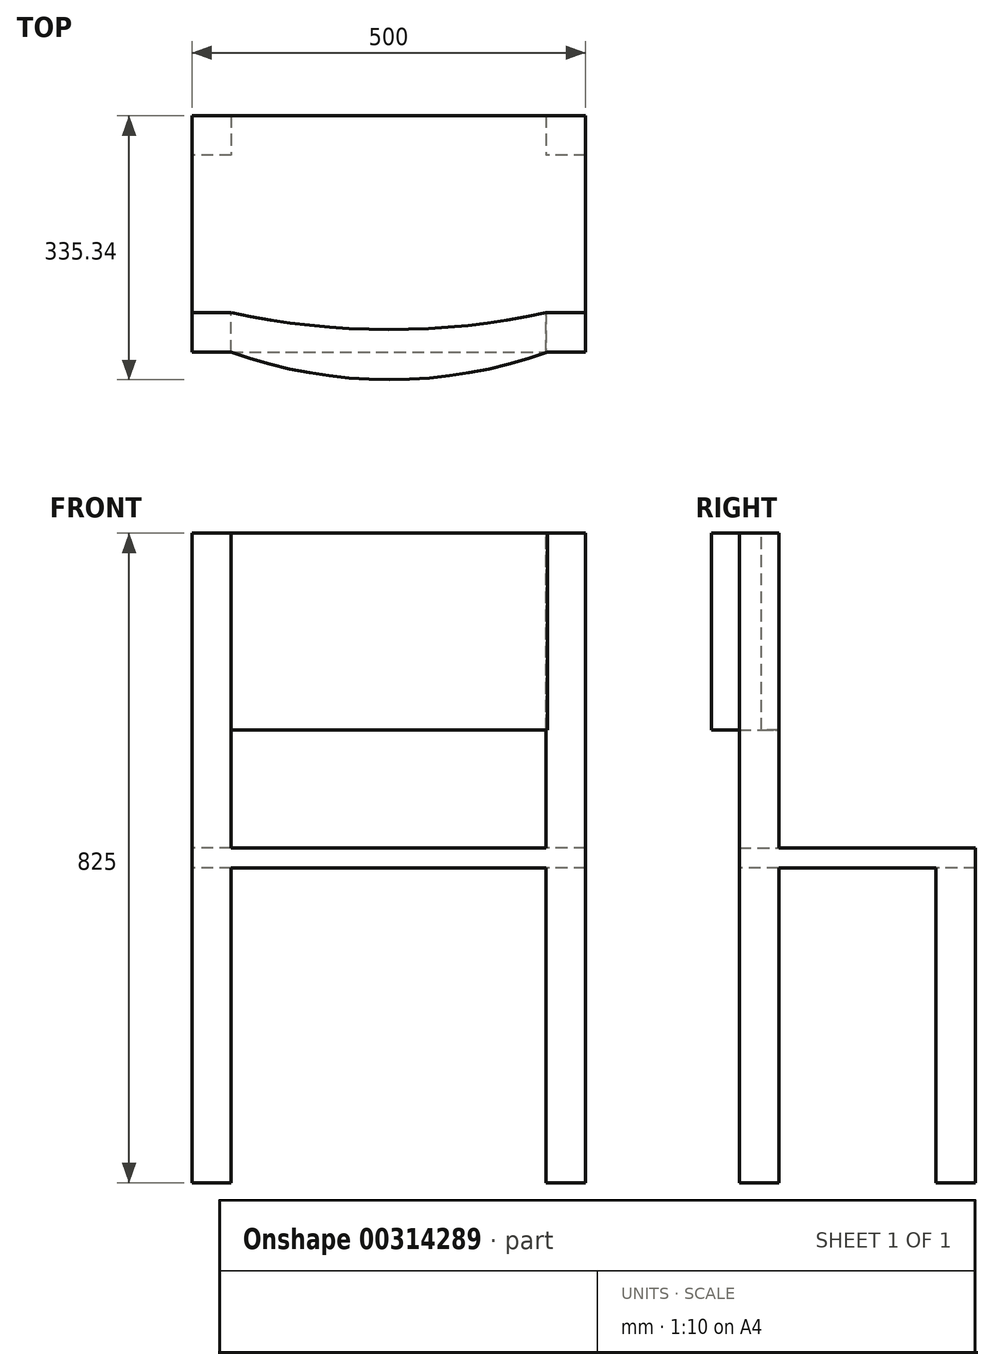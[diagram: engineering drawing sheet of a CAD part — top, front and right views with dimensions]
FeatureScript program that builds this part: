
annotation { "Feature Type Name" : "Feature", "Feature Type Description" : "" }
export const myFeature = defineFeature(function(context is Context, id is Id, definition is map)
    precondition{}
    {
        {
            var Q0;
            Q0=qCreatedBy(makeId("Top.planeOp"),FACE);
            var sketch = newSketch(context, id + "F0", { "sketchPlane" : qUnion([Q0])});
            skLineSegment(sketch, "E0.bottom", {"start": v(-295.12, 76.38) * mm, "end": v(204.88, 76.38) * mm});
            skLineSegment(sketch, "E0.top", {"start": v(-295.12, -223.62) * mm, "end": v(204.88, -223.62) * mm});
            skLineSegment(sketch, "E0.left", {"start": v(-295.12, 76.38) * mm, "end": v(-295.12, -223.62) * mm});
            skLineSegment(sketch, "E0.right", {"start": v(204.88, 76.38) * mm, "end": v(204.88, -223.62) * mm});
            skSolve(sketch);
        }
        {
            var Q0;
            Q0=makeQuery(id+"F0.imprint","IMPRINT",FACE,{"disambiguationData":[TD([[makeQuery(id+"F0.imprint","IMPRINT",EDGE,{"derivedFrom":sQuery(id+"F0.wireOp",EDGE,"E0.bottom")}),-1.0]])]});
            extrude(context, id + "F1", {"entities" : qUnion([Q0]), "depth" : 25 * mm});
        }
        {
            var Q0;
            Q0=makeQuery(id+"F1.opExtrude","CAP_FACE",FACE,{"disambiguationData":[OSD([sQuery(id+"F0.wireOp",EDGE,"E0.bottom"),sQuery(id+"F0.wireOp",EDGE,"E0.top"),sQuery(id+"F0.wireOp",EDGE,"E0.left"),sQuery(id+"F0.wireOp",EDGE,"E0.right")])],"isStart":true});
            var sketch = newSketch(context, id + "F2", { "sketchPlane" : qUnion([Q0])});
            skLineSegment(sketch, "E1.bottom", {"start": v(204.88, -76.38) * mm, "end": v(154.88, -76.38) * mm});
            skLineSegment(sketch, "E1.top", {"start": v(204.88, -26.38) * mm, "end": v(154.88, -26.38) * mm});
            skLineSegment(sketch, "E1.left", {"start": v(204.88, -76.38) * mm, "end": v(204.88, -26.38) * mm});
            skLineSegment(sketch, "E1.right", {"start": v(154.88, -76.38) * mm, "end": v(154.88, -26.38) * mm});
            skLineSegment(sketch, "E2.bottom", {"start": v(-245.12, -76.38) * mm, "end": v(-295.12, -76.38) * mm});
            skLineSegment(sketch, "E2.top", {"start": v(-245.12, -26.38) * mm, "end": v(-295.12, -26.38) * mm});
            skLineSegment(sketch, "E2.left", {"start": v(-245.12, -76.38) * mm, "end": v(-245.12, -26.38) * mm});
            skLineSegment(sketch, "E2.right", {"start": v(-295.12, -76.38) * mm, "end": v(-295.12, -26.38) * mm});
            skLineSegment(sketch, "E3.bottom", {"start": v(204.88, 173.62) * mm, "end": v(154.88, 173.62) * mm});
            skLineSegment(sketch, "E3.top", {"start": v(204.88, 223.62) * mm, "end": v(154.88, 223.62) * mm});
            skLineSegment(sketch, "E3.left", {"start": v(204.88, 173.62) * mm, "end": v(204.88, 223.62) * mm});
            skLineSegment(sketch, "E3.right", {"start": v(154.88, 173.62) * mm, "end": v(154.88, 223.62) * mm});
            skLineSegment(sketch, "E4.bottom", {"start": v(-245.12, 173.62) * mm, "end": v(-295.12, 173.62) * mm});
            skLineSegment(sketch, "E4.top", {"start": v(-245.12, 223.62) * mm, "end": v(-295.12, 223.62) * mm});
            skLineSegment(sketch, "E4.left", {"start": v(-245.12, 173.62) * mm, "end": v(-245.12, 223.62) * mm});
            skLineSegment(sketch, "E4.right", {"start": v(-295.12, 173.62) * mm, "end": v(-295.12, 223.62) * mm});
            skSolve(sketch);
        }
        {
            var Q0;
            Q0=makeQuery(id+"F2.imprint","IMPRINT",FACE,{"disambiguationData":[TD([[makeQuery(id+"F2.imprint","IMPRINT",EDGE,{"derivedFrom":sQuery(id+"F2.wireOp",EDGE,"E1.bottom")}),1.0]])]});
            var Q1;
            Q1=makeQuery(id+"F2.imprint","IMPRINT",FACE,{"disambiguationData":[TD([[makeQuery(id+"F2.imprint","IMPRINT",EDGE,{"derivedFrom":sQuery(id+"F2.wireOp",EDGE,"E3.bottom")}),-1.0]])]});
            var Q2;
            Q2=makeQuery(id+"F2.imprint","IMPRINT",FACE,{"disambiguationData":[TD([[makeQuery(id+"F2.imprint","IMPRINT",EDGE,{"derivedFrom":sQuery(id+"F2.wireOp",EDGE,"E2.bottom")}),1.0]])]});
            var Q3;
            Q3=makeQuery(id+"F2.imprint","IMPRINT",FACE,{"disambiguationData":[TD([[makeQuery(id+"F2.imprint","IMPRINT",EDGE,{"derivedFrom":sQuery(id+"F2.wireOp",EDGE,"E4.bottom")}),-1.0]])]});
            extrude(context, id + "F3", {"entities" : qUnion([Q0, Q1, Q2, Q3]), "operationType" : NewBodyOperationType.ADD, "depth" : 400 * mm});
        }
        {
            var Q0;
            Q0=makeQuery(id+"F1.opExtrude","CAP_FACE",FACE,{"disambiguationData":[OSD([sQuery(id+"F0.wireOp",EDGE,"E0.bottom"),sQuery(id+"F0.wireOp",EDGE,"E0.top"),sQuery(id+"F0.wireOp",EDGE,"E0.left"),sQuery(id+"F0.wireOp",EDGE,"E0.right")])],"isStart":false});
            var sketch = newSketch(context, id + "F4", { "sketchPlane" : qUnion([Q0])});
            skLineSegment(sketch, "E5.bottom", {"start": v(204.88, -223.62) * mm, "end": v(154.88, -223.62) * mm});
            skLineSegment(sketch, "E5.top", {"start": v(204.88, -173.62) * mm, "end": v(154.88, -173.62) * mm});
            skLineSegment(sketch, "E5.left", {"start": v(204.88, -223.62) * mm, "end": v(204.88, -173.62) * mm});
            skLineSegment(sketch, "E5.right", {"start": v(154.88, -223.62) * mm, "end": v(154.88, -173.62) * mm});
            skLineSegment(sketch, "E6.bottom", {"start": v(-245.12, -223.62) * mm, "end": v(-295.12, -223.62) * mm});
            skLineSegment(sketch, "E6.top", {"start": v(-245.12, -173.62) * mm, "end": v(-295.12, -173.62) * mm});
            skLineSegment(sketch, "E6.left", {"start": v(-245.12, -223.62) * mm, "end": v(-245.12, -173.62) * mm});
            skLineSegment(sketch, "E6.right", {"start": v(-295.12, -223.62) * mm, "end": v(-295.12, -173.62) * mm});
            skSolve(sketch);
        }
        {
            var Q0;
            Q0=makeQuery(id+"F4.imprint","IMPRINT",FACE,{"disambiguationData":[TD([[makeQuery(id+"F4.imprint","IMPRINT",EDGE,{"derivedFrom":sQuery(id+"F4.wireOp",EDGE,"E5.bottom")}),1.0]])]});
            var Q1;
            Q1=makeQuery(id+"F4.imprint","IMPRINT",FACE,{"disambiguationData":[TD([[makeQuery(id+"F4.imprint","IMPRINT",EDGE,{"derivedFrom":sQuery(id+"F4.wireOp",EDGE,"E6.bottom")}),1.0]])]});
            extrude(context, id + "F5", {"entities" : qUnion([Q0, Q1]), "operationType" : NewBodyOperationType.ADD, "depth" : 400 * mm});
        }
        {
            var Q0;
            Q0=makeQuery(id+"F5.opExtrude","CAP_FACE",FACE,{"disambiguationData":[OSD([sQuery(id+"F4.wireOp",EDGE,"E6.bottom"),sQuery(id+"F4.wireOp",EDGE,"E6.top"),sQuery(id+"F4.wireOp",EDGE,"E6.left"),sQuery(id+"F4.wireOp",EDGE,"E6.right")])],"isStart":false});
            var sketch = newSketch(context, id + "F6", { "sketchPlane" : qUnion([Q0])});
            skArc(sketch, "E7", {"start": v(-245.12, -223.62) * mm, "mid": v(-44.39, -258.96) * mm, "end": v(156.34, -223.62) * mm});
            skArc(sketch, "E8", {"start": v(-245.12, -173.62) * mm, "mid": v(-44.85, -195.25) * mm, "end": v(155.42, -173.62) * mm});
            skLineSegment(sketch, "E9", {"start": v(-245.12, -223.62) * mm, "end": v(-245.12, -173.62) * mm});
            skLineSegment(sketch, "E10", {"start": v(156.34, -223.62) * mm, "end": v(155.42, -173.62) * mm});
            skSolve(sketch);
        }
        {
            var Q0;
            Q0=makeQuery(id+"F6.imprint","IMPRINT",FACE,{"disambiguationData":[TD([[makeQuery(id+"F6.imprint","IMPRINT",EDGE,{"derivedFrom":sQuery(id+"F6.wireOp",EDGE,"E7")}),1.0]])]});
            extrude(context, id + "F7", {"entities" : qUnion([Q0]), "operationType" : NewBodyOperationType.ADD, "oppositeDirection" : true, "depth" : 250 * mm});
        }
    });
